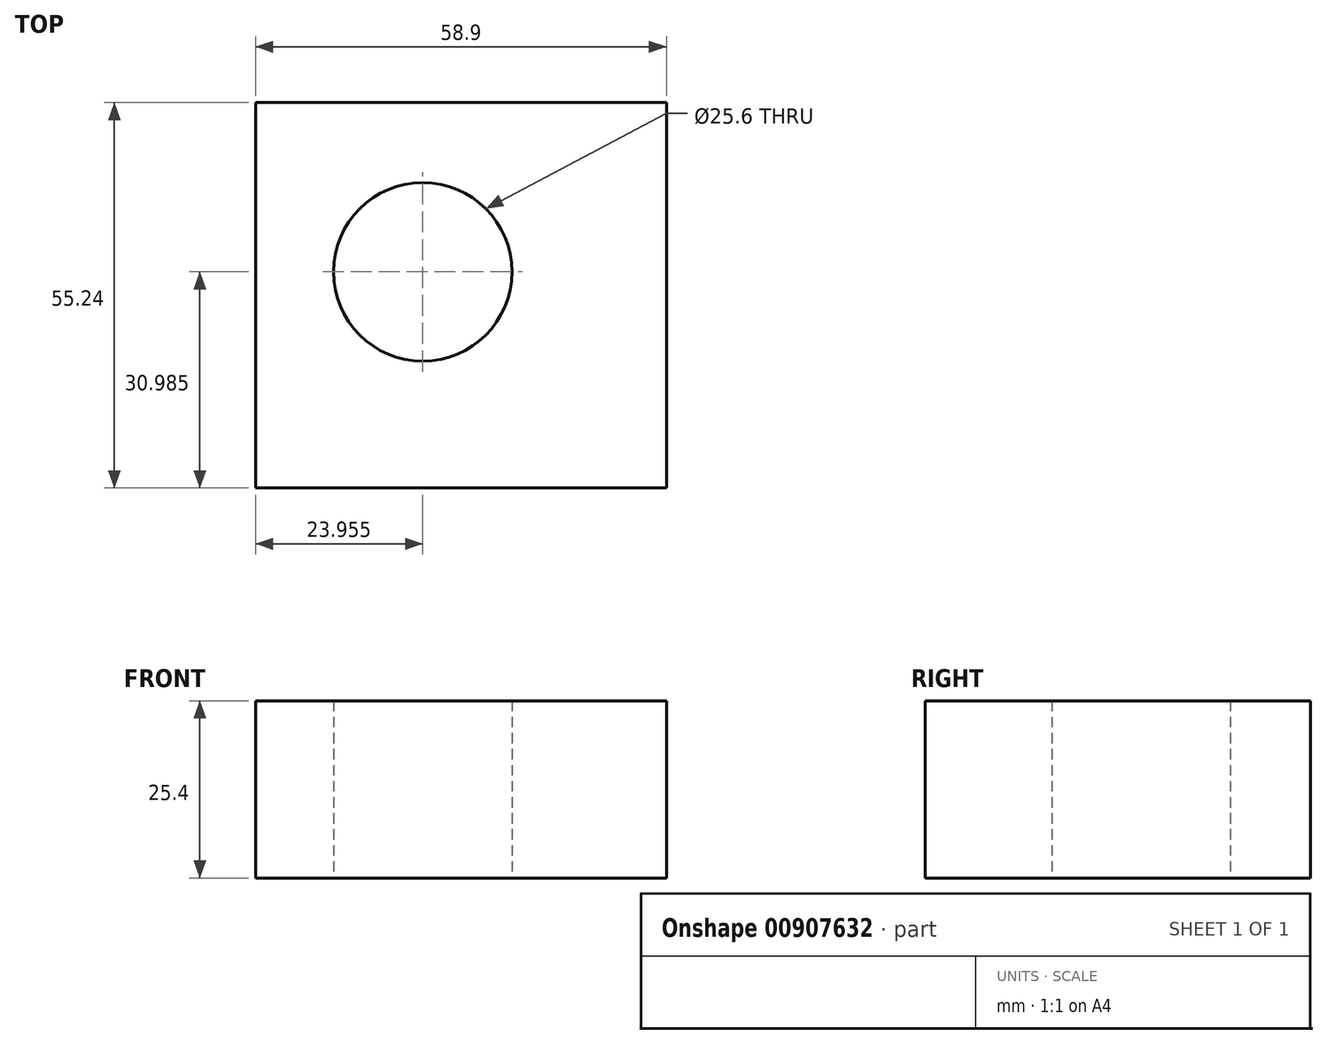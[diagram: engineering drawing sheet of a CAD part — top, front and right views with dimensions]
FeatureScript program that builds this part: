
annotation { "Feature Type Name" : "Feature", "Feature Type Description" : "" }
export const myFeature = defineFeature(function(context is Context, id is Id, definition is map)
    precondition{}
    {
        {
            var Q0;
            Q0=qCreatedBy(makeId("Top.planeOp"),FACE);
            var sketch = newSketch(context, id + "F0", { "sketchPlane" : qUnion([Q0])});
            skLineSegment(sketch, "E0.bottom", {"start": v(-87, 35.6) * mm, "end": v(-28.1, 35.6) * mm});
            skLineSegment(sketch, "E0.top", {"start": v(-87, -19.64) * mm, "end": v(-28.1, -19.64) * mm});
            skLineSegment(sketch, "E0.left", {"start": v(-87, 35.6) * mm, "end": v(-87, -19.64) * mm});
            skLineSegment(sketch, "E0.right", {"start": v(-28.1, 35.6) * mm, "end": v(-28.1, -19.64) * mm});
            skCircle(sketch, "E1", {"center": v(13.55, 32.26) * mm, "radius": 21.03 * mm});
            skLineSegment(sketch, "E2", {"start": v(-8.65, -12.96) * mm, "end": v(30.44, -58.03) * mm});
            skLineSegment(sketch, "E3", {"start": v(30.44, -58.03) * mm, "end": v(54.72, -25.26) * mm});
            skLineSegment(sketch, "E4", {"start": v(54.72, -25.26) * mm, "end": v(34.63, 8.06) * mm});
            skLineSegment(sketch, "E5", {"start": v(34.63, 8.06) * mm, "end": v(-8.65, -12.96) * mm});
            skCircle(sketch, "E6", {"center": v(-63.05, 11.34) * mm, "radius": 12.8 * mm});
            skSolve(sketch);
        }
        {
            var Q0;
            Q0=makeQuery(id+"F0.imprint","IMPRINT",FACE,{"disambiguationData":[TD([[makeQuery(id+"F0.imprint","IMPRINT",EDGE,{"derivedFrom":sQuery(id+"F0.wireOp",EDGE,"E0.bottom")}),-1.0]])]});
            extrude(context, id + "F1", {"entities" : qUnion([Q0]), "depth" : 25.4 * mm, "offsetDistance" : 25.4 * mm});
        }
    });
